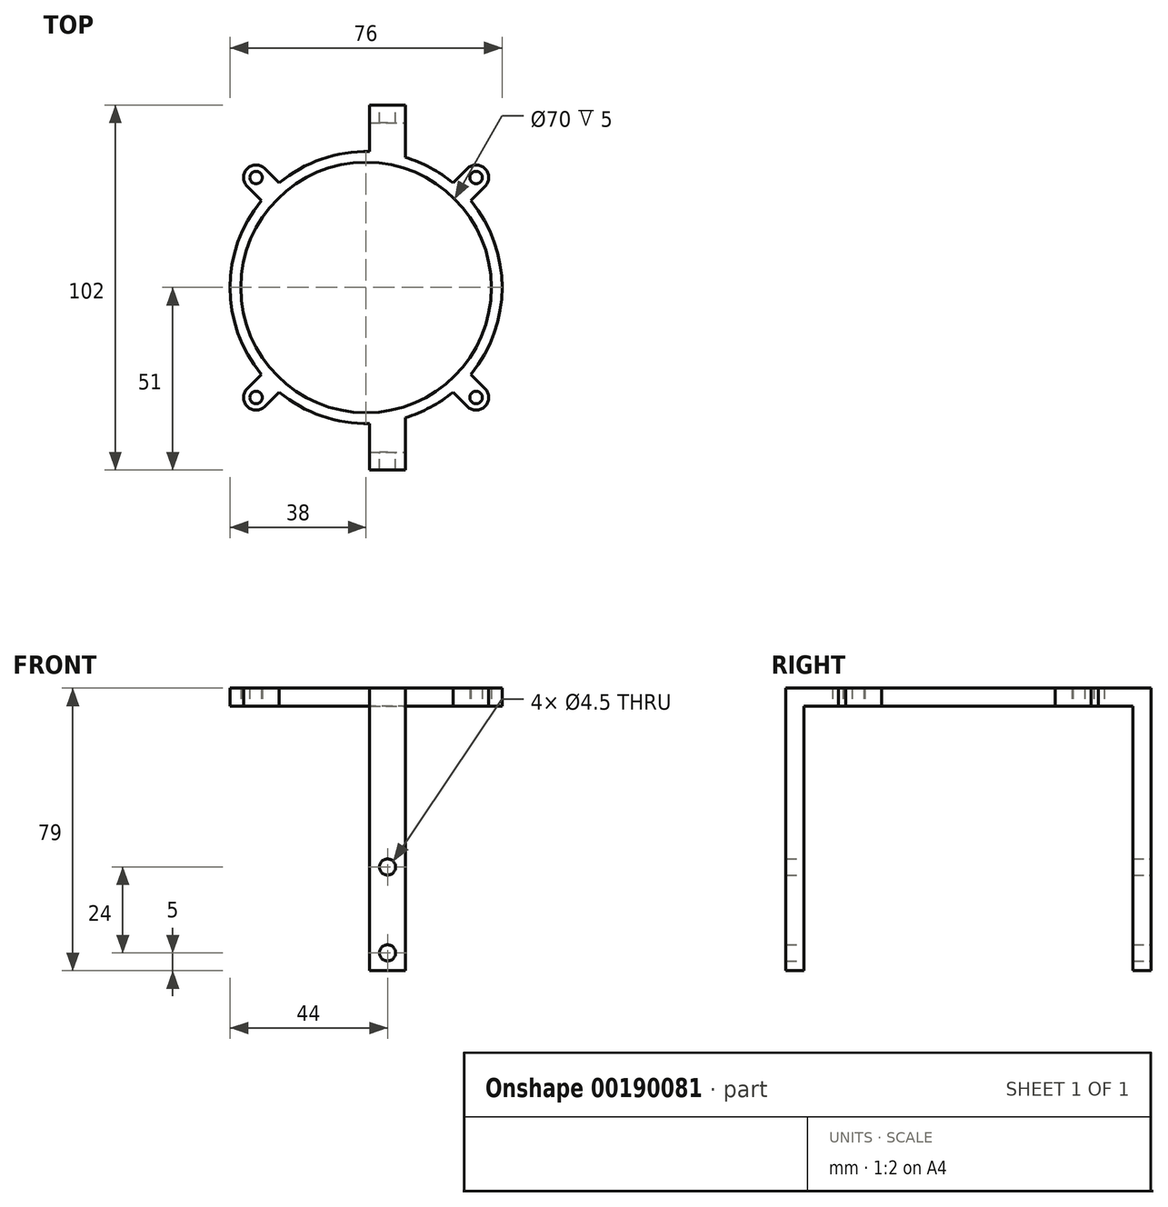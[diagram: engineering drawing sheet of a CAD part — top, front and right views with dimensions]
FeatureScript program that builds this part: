
annotation { "Feature Type Name" : "Feature", "Feature Type Description" : "" }
export const myFeature = defineFeature(function(context is Context, id is Id, definition is map)
    precondition{}
    {
        {
            var Q0;
            Q0=qCreatedBy(makeId("Top.planeOp"),FACE);
            var sketch = newSketch(context, id + "F0", { "sketchPlane" : qUnion([Q0])});
            skCircle(sketch, "E0", {"center": v(0, 0) * mm, "radius": 35 * mm});
            skCircle(sketch, "E1", {"center": v(30.75, 30.75) * mm, "radius": 1.75 * mm});
            skLineSegment(sketch, "E2", {"start": v(30.75, 30.75) * mm, "end": v(0, 30.75) * mm, "construction": true});
            skLineSegment(sketch, "E3", {"start": v(30.75, 30.75) * mm, "end": v(30.75, 0) * mm, "construction": true});
            skLineSegment(sketch, "E4", {"start": v(30.75, 0) * mm, "end": v(30.75, 6.23) * mm, "construction": true});
            skLineSegment(sketch, "E5", {"start": v(0, 0) * mm, "end": v(0, 23.3) * mm, "construction": true});
            skLineSegment(sketch, "E6", {"start": v(0, 0) * mm, "end": v(17.07, 0) * mm, "construction": true});
            skCircle(sketch, "E7.MirrorC", {"center": v(-30.75, 30.75) * mm, "radius": 1.75 * mm});
            skCircle(sketch, "E8.MirrorC", {"center": v(-30.75, -30.75) * mm, "radius": 1.75 * mm});
            skCircle(sketch, "E9.MirrorC", {"center": v(30.75, -30.75) * mm, "radius": 1.75 * mm});
            skArc(sketch, "E10", {"start": v(-28.28, 33.22) * mm, "mid": v(-33.22, 33.22) * mm, "end": v(-33.22, 28.28) * mm});
            skLineSegment(sketch, "E11", {"start": v(-30.75, 30.75) * mm, "end": v(0, 0) * mm, "construction": true});
            skLineSegment(sketch, "E12", {"start": v(-28.28, 33.22) * mm, "end": v(-24.28, 29.23) * mm});
            skArc(sketch, "E13", {"start": v(-24.28, 29.23) * mm, "mid": v(-12.9, 35.74) * mm, "end": v(0, 38) * mm});
            skLineSegment(sketch, "E14.MirrorCS", {"start": v(-33.22, 28.28) * mm, "end": v(-29.23, 24.28) * mm});
            skArc(sketch, "E15.MirrorCS", {"start": v(-29.23, 24.28) * mm, "mid": v(-35.74, 12.9) * mm, "end": v(-38, 0) * mm});
            skArc(sketch, "E16.MirrorCS", {"start": v(29.23, 24.28) * mm, "mid": v(35.74, 12.9) * mm, "end": v(38, 0) * mm});
            skLineSegment(sketch, "E17.MirrorCS", {"start": v(33.22, 28.28) * mm, "end": v(29.23, 24.28) * mm});
            skArc(sketch, "E18.MirrorCS", {"start": v(28.28, 33.22) * mm, "mid": v(33.22, 33.22) * mm, "end": v(33.22, 28.28) * mm});
            skLineSegment(sketch, "E19.MirrorCS", {"start": v(28.28, 33.22) * mm, "end": v(24.28, 29.23) * mm});
            skArc(sketch, "E20.MirrorCS", {"start": v(24.28, 29.23) * mm, "mid": v(12.9, 35.74) * mm, "end": v(0, 38) * mm});
            skArc(sketch, "E21.MirrorCS", {"start": v(-29.23, -24.28) * mm, "mid": v(-35.74, -12.9) * mm, "end": v(-38, 0) * mm});
            skLineSegment(sketch, "E22.MirrorCS", {"start": v(-33.22, -28.28) * mm, "end": v(-29.23, -24.28) * mm});
            skArc(sketch, "E23.MirrorCS", {"start": v(-28.28, -33.22) * mm, "mid": v(-33.22, -33.22) * mm, "end": v(-33.22, -28.28) * mm});
            skLineSegment(sketch, "E24.MirrorCS", {"start": v(-28.28, -33.22) * mm, "end": v(-24.28, -29.23) * mm});
            skArc(sketch, "E25.MirrorCS", {"start": v(-24.28, -29.23) * mm, "mid": v(-12.9, -35.74) * mm, "end": v(0, -38) * mm});
            skArc(sketch, "E26.MirrorCS", {"start": v(24.28, -29.23) * mm, "mid": v(12.9, -35.74) * mm, "end": v(0, -38) * mm});
            skLineSegment(sketch, "E27.MirrorCS", {"start": v(28.28, -33.22) * mm, "end": v(24.28, -29.23) * mm});
            skArc(sketch, "E28.MirrorCS", {"start": v(28.28, -33.22) * mm, "mid": v(33.22, -33.22) * mm, "end": v(33.22, -28.28) * mm});
            skLineSegment(sketch, "E29.MirrorCS", {"start": v(33.22, -28.28) * mm, "end": v(29.23, -24.28) * mm});
            skArc(sketch, "E30.MirrorCS", {"start": v(29.23, -24.28) * mm, "mid": v(35.74, -12.9) * mm, "end": v(38, 0) * mm});
            skLineSegment(sketch, "E31", {"start": v(1, 51) * mm, "end": v(11, 51) * mm});
            skLineSegment(sketch, "E32", {"start": v(1, 51) * mm, "end": v(1, 37.99) * mm});
            skLineSegment(sketch, "E33.MirrorCS", {"start": v(1, -51) * mm, "end": v(1, -37.99) * mm});
            skLineSegment(sketch, "E34.MirrorCS", {"start": v(1, -51) * mm, "end": v(11, -51) * mm});
            skLineSegment(sketch, "E35", {"start": v(6, -51) * mm, "end": v(6, -42.44) * mm, "construction": true});
            skLineSegment(sketch, "E36", {"start": v(11, 51) * mm, "end": v(11, 36.37) * mm});
            skLineSegment(sketch, "E37", {"start": v(11, -51) * mm, "end": v(11, -36.37) * mm});
            skSolve(sketch);
        }
        {
            var Q0;
            Q0 = qSketchRegion(id + "F0", true);
            extrude(context, id + "F1", {"entities" : qUnion([Q0]), "depth" : 5 * mm});
        }
        {
            var Q0;
            Q0=makeQuery(id+"F1.opExtrude","CAP_FACE",FACE,{"disambiguationData":[OSD([sQuery(id+"F0.wireOp",EDGE,"E0"),sQuery(id+"F0.wireOp",EDGE,"E1"),sQuery(id+"F0.wireOp",EDGE,"E7.MirrorC"),sQuery(id+"F0.wireOp",EDGE,"E8.MirrorC"),sQuery(id+"F0.wireOp",EDGE,"E9.MirrorC"),sQuery(id+"F0.wireOp",EDGE,"E10"),sQuery(id+"F0.wireOp",EDGE,"E12"),sQuery(id+"F0.wireOp",EDGE,"E13"),sQuery(id+"F0.wireOp",EDGE,"E14.MirrorCS"),sQuery(id+"F0.wireOp",EDGE,"E15.MirrorCS"),sQuery(id+"F0.wireOp",EDGE,"E16.MirrorCS"),sQuery(id+"F0.wireOp",EDGE,"E17.MirrorCS"),sQuery(id+"F0.wireOp",EDGE,"E18.MirrorCS"),sQuery(id+"F0.wireOp",EDGE,"E19.MirrorCS"),sQuery(id+"F0.wireOp",EDGE,"E20.MirrorCS"),sQuery(id+"F0.wireOp",EDGE,"E21.MirrorCS"),sQuery(id+"F0.wireOp",EDGE,"E22.MirrorCS"),sQuery(id+"F0.wireOp",EDGE,"E23.MirrorCS"),sQuery(id+"F0.wireOp",EDGE,"E24.MirrorCS"),sQuery(id+"F0.wireOp",EDGE,"E25.MirrorCS"),sQuery(id+"F0.wireOp",EDGE,"E26.MirrorCS"),sQuery(id+"F0.wireOp",EDGE,"E27.MirrorCS"),sQuery(id+"F0.wireOp",EDGE,"E28.MirrorCS"),sQuery(id+"F0.wireOp",EDGE,"E29.MirrorCS"),sQuery(id+"F0.wireOp",EDGE,"E30.MirrorCS"),sQuery(id+"F0.wireOp",EDGE,"E31"),sQuery(id+"F0.wireOp",EDGE,"E32"),sQuery(id+"F0.wireOp",EDGE,"E33.MirrorCS"),sQuery(id+"F0.wireOp",EDGE,"E34.MirrorCS"),sQuery(id+"F0.wireOp",EDGE,"E36"),sQuery(id+"F0.wireOp",EDGE,"E37")])],"isStart":true});
            var sketch = newSketch(context, id + "F2", { "sketchPlane" : qUnion([Q0])});
            skLineSegment(sketch, "E38", {"start": v(11, -51) * mm, "end": v(1, -51) * mm});
            skLineSegment(sketch, "E39", {"start": v(1, -51) * mm, "end": v(1, -46) * mm});
            skLineSegment(sketch, "E40", {"start": v(1, -46) * mm, "end": v(11, -46) * mm});
            skLineSegment(sketch, "E41", {"start": v(11, -46) * mm, "end": v(11, -51) * mm});
            skLineSegment(sketch, "E42", {"start": v(0, 0) * mm, "end": v(-6.4, 0) * mm, "construction": true});
            skLineSegment(sketch, "E43.MirrorCS", {"start": v(1, 46) * mm, "end": v(11, 46) * mm});
            skLineSegment(sketch, "E44.MirrorCS", {"start": v(11, 46) * mm, "end": v(11, 51) * mm});
            skLineSegment(sketch, "E45.MirrorCS", {"start": v(11, 51) * mm, "end": v(1, 51) * mm});
            skLineSegment(sketch, "E46.MirrorCS", {"start": v(1, 51) * mm, "end": v(1, 46) * mm});
            skSolve(sketch);
        }
        {
            var Q0;
            Q0 = qSketchRegion(id + "F2", true);
            extrude(context, id + "F3", {"entities" : qUnion([Q0]), "operationType" : NewBodyOperationType.ADD, "depth" : 74 * mm});
        }
        {
            var Q0;
            Q0=makeQuery(id+"F3.boolean.opBoolean","MERGE",FACE,{"derivedFrom":[makeQuery(id+"F1.opExtrude","SWEPT_FACE",FACE,{"disambiguationData":[OSD([sQuery(id+"F0.wireOp",EDGE,"E31")])]}),makeQuery(id+"F3.opExtrude","SWEPT_FACE",FACE,{"disambiguationData":[OSD([sQuery(id+"F2.wireOp",EDGE,"VEnWywbk-bPfA-C2nd-fkCd-7Hp5rDAqdaRL")])]})]});
            var sketch = newSketch(context, id + "F4", { "sketchPlane" : qUnion([Q0])});
            skCircle(sketch, "E47", {"center": v(-6, -69) * mm, "radius": 2.25 * mm});
            skPoint(sketch, "E47.centerSnap0", {"position": v(-6, -74) * mm});
            skCircle(sketch, "E48", {"center": v(-6, -45) * mm, "radius": 2.25 * mm});
            skSolve(sketch);
        }
        {
            var Q0;
            Q0 = qSketchRegion(id + "F4", true);
            extrude(context, id + "F5", {"entities" : qUnion([Q0]), "operationType" : NewBodyOperationType.REMOVE, "endBound" : BoundingType.THROUGH_ALL, "oppositeDirection" : true, "depth" : 25 * mm});
        }
    });
